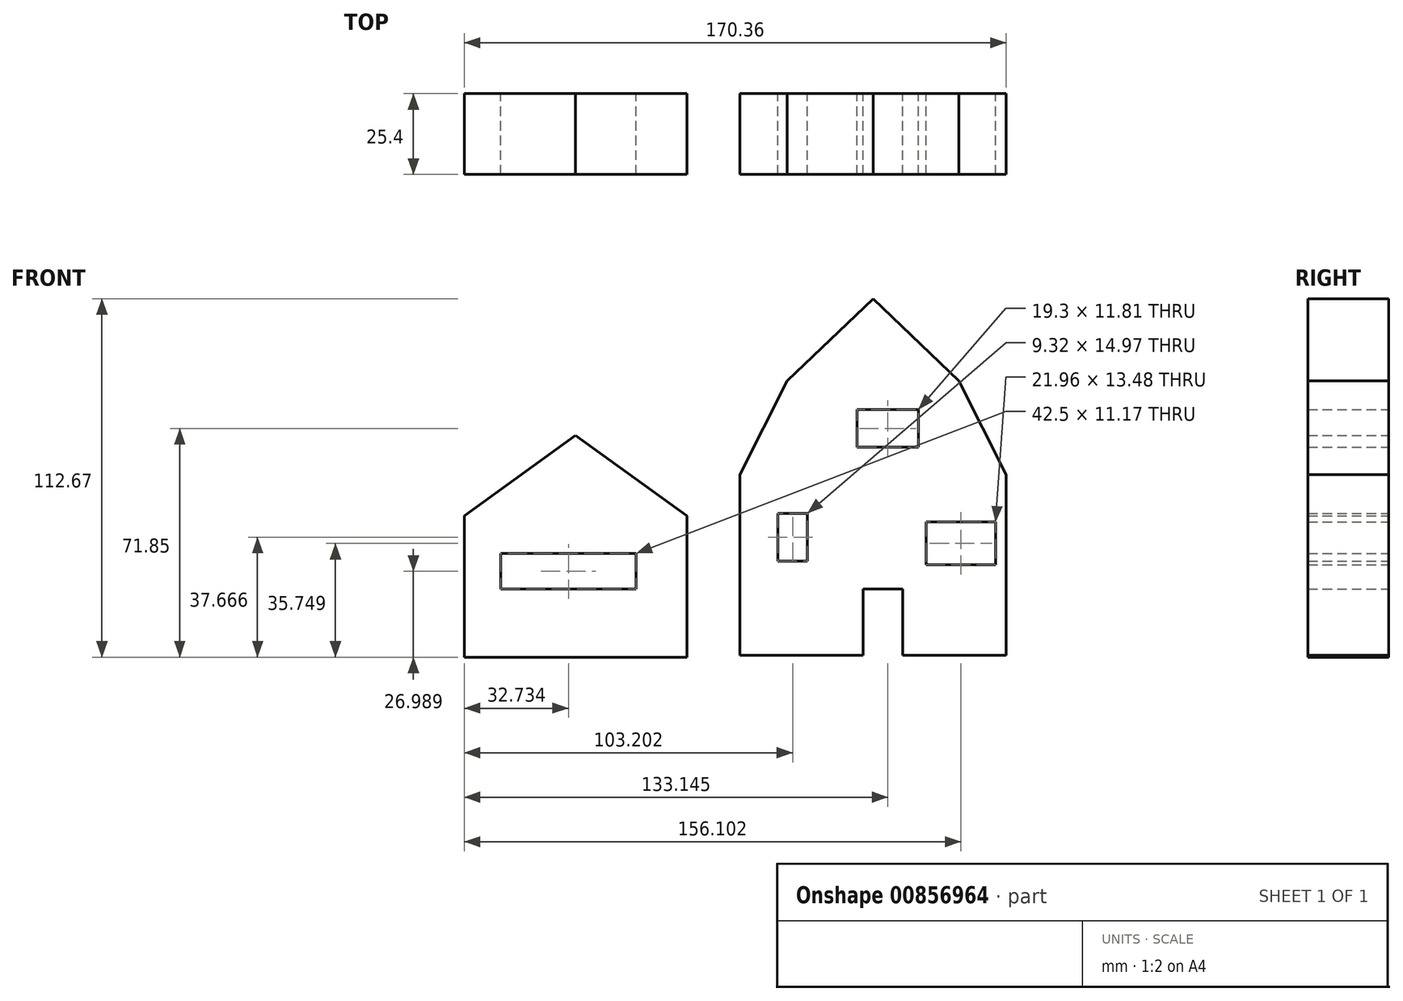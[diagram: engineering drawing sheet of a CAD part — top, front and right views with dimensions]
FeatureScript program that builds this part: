
annotation { "Feature Type Name" : "Feature", "Feature Type Description" : "" }
export const myFeature = defineFeature(function(context is Context, id is Id, definition is map)
    precondition{}
    {
        {
            var Q0;
            Q0=qCreatedBy(makeId("Front.planeOp"),FACE);
            var sketch = newSketch(context, id + "F0", { "sketchPlane" : qUnion([Q0])});
            skLineSegment(sketch, "E0.bottom", {"start": v(-4.1, 6.25) * mm, "end": v(79.64, 6.25) * mm});
            skLineSegment(sketch, "E0.top", {"start": v(-4.1, -50.52) * mm, "end": v(79.64, -50.52) * mm});
            skLineSegment(sketch, "E0.left", {"start": v(-4.1, 6.25) * mm, "end": v(-4.1, -50.52) * mm});
            skLineSegment(sketch, "E0.right", {"start": v(79.64, 6.25) * mm, "end": v(79.64, -50.52) * mm});
            skLineSegment(sketch, "E1", {"start": v(-4.1, 6.25) * mm, "end": v(10.78, 35.73) * mm});
            skLineSegment(sketch, "E2", {"start": v(10.78, 35.73) * mm, "end": v(64.75, 35.73) * mm});
            skLineSegment(sketch, "E3", {"start": v(64.75, 35.73) * mm, "end": v(79.64, 6.25) * mm});
            skLineSegment(sketch, "E4", {"start": v(10.78, 35.73) * mm, "end": v(37.76, 61.53) * mm});
            skLineSegment(sketch, "E5", {"start": v(37.76, 61.53) * mm, "end": v(64.75, 35.73) * mm});
            skLineSegment(sketch, "E6.bottom", {"start": v(-90.72, -6.78) * mm, "end": v(-20.78, -6.78) * mm});
            skLineSegment(sketch, "E6.top", {"start": v(-90.72, -51.14) * mm, "end": v(-20.78, -51.14) * mm});
            skLineSegment(sketch, "E6.left", {"start": v(-90.72, -6.78) * mm, "end": v(-90.72, -51.14) * mm});
            skLineSegment(sketch, "E6.right", {"start": v(-20.78, -6.78) * mm, "end": v(-20.78, -51.14) * mm});
            skLineSegment(sketch, "E7", {"start": v(-90.72, -6.78) * mm, "end": v(-55.75, 18.56) * mm});
            skLineSegment(sketch, "E8", {"start": v(-55.75, 18.56) * mm, "end": v(-20.78, -6.78) * mm});
            skLineSegment(sketch, "E9", {"start": v(-79.24, -51.14) * mm, "end": v(-79.24, -18.57) * mm});
            skLineSegment(sketch, "E10", {"start": v(-79.24, -18.57) * mm, "end": v(-36.74, -18.57) * mm});
            skLineSegment(sketch, "E11", {"start": v(-36.74, -18.57) * mm, "end": v(-36.74, -51.14) * mm});
            skLineSegment(sketch, "E12", {"start": v(34.67, -50.52) * mm, "end": v(34.67, -29.73) * mm});
            skLineSegment(sketch, "E13", {"start": v(34.67, -29.73) * mm, "end": v(47.08, -29.73) * mm});
            skLineSegment(sketch, "E14", {"start": v(47.08, -29.73) * mm, "end": v(47.08, -50.52) * mm});
            skLineSegment(sketch, "E15", {"start": v(-79.24, -29.74) * mm, "end": v(-36.74, -29.74) * mm});
            skLineSegment(sketch, "E16", {"start": v(-36.74, -29.74) * mm, "end": v(-45.42, -29.74) * mm});
            skLineSegment(sketch, "E17", {"start": v(-45.42, -29.74) * mm, "end": v(-45.42, -18.57) * mm});
            skLineSegment(sketch, "E18", {"start": v(-53.18, -29.74) * mm, "end": v(-53.18, -18.57) * mm});
            skLineSegment(sketch, "E19", {"start": v(-61.55, -29.74) * mm, "end": v(-61.55, -18.57) * mm});
            skLineSegment(sketch, "E20", {"start": v(-70.24, -29.74) * mm, "end": v(-70.24, -18.57) * mm});
            skLineSegment(sketch, "E21.bottom", {"start": v(32.78, 26.61) * mm, "end": v(52.07, 26.61) * mm});
            skLineSegment(sketch, "E21.top", {"start": v(32.78, 14.8) * mm, "end": v(52.07, 14.8) * mm});
            skLineSegment(sketch, "E21.left", {"start": v(32.78, 26.61) * mm, "end": v(32.78, 14.8) * mm});
            skLineSegment(sketch, "E21.right", {"start": v(52.07, 26.61) * mm, "end": v(52.07, 14.8) * mm});
            skLineSegment(sketch, "E22.bottom", {"start": v(7.82, -5.99) * mm, "end": v(17.14, -5.99) * mm});
            skLineSegment(sketch, "E22.top", {"start": v(7.82, -20.96) * mm, "end": v(17.14, -20.96) * mm});
            skLineSegment(sketch, "E22.left", {"start": v(7.82, -5.99) * mm, "end": v(7.82, -20.96) * mm});
            skLineSegment(sketch, "E22.right", {"start": v(17.14, -5.99) * mm, "end": v(17.14, -20.96) * mm});
            skPoint(sketch, "E23.oppositeSnap0", {"position": v(79.64, -22.13) * mm});
            skLineSegment(sketch, "E23.bottom", {"start": v(54.4, -8.65) * mm, "end": v(76.36, -8.65) * mm});
            skLineSegment(sketch, "E23.top", {"start": v(54.4, -22.13) * mm, "end": v(76.36, -22.13) * mm});
            skLineSegment(sketch, "E23.left", {"start": v(54.4, -8.65) * mm, "end": v(54.4, -22.13) * mm});
            skLineSegment(sketch, "E23.right", {"start": v(76.36, -8.65) * mm, "end": v(76.36, -22.13) * mm});
            skLineSegment(sketch, "E24.bottom", {"start": v(42.43, 26.61) * mm, "end": v(32.78, 26.61) * mm});
            skLineSegment(sketch, "E24.top", {"start": v(42.43, 26.61) * mm, "end": v(32.78, 26.61) * mm});
            skLineSegment(sketch, "E24.left", {"start": v(42.43, 26.61) * mm, "end": v(42.43, 26.61) * mm});
            skLineSegment(sketch, "E24.right", {"start": v(32.78, 26.61) * mm, "end": v(32.78, 26.61) * mm});
            skSolve(sketch);
        }
        {
            var Q0;
            Q0=makeQuery(id+"F0.imprint","IMPRINT",FACE,{"disambiguationData":[TD([[makeQuery(id+"F0.imprint","IMPRINT",EDGE,{"derivedFrom":sQuery(id+"F0.wireOp",EDGE,"E2")}),1.0]])]});
            var Q1;
            Q1=makeQuery(id+"F0.imprint","IMPRINT",FACE,{"disambiguationData":[TD([[makeQuery(id+"F0.imprint","IMPRINT",EDGE,{"derivedFrom":sQuery(id+"F0.wireOp",EDGE,"E6.bottom")}),1.0]])]});
            var Q2;
            Q2=makeQuery(id+"F0.imprint","IMPRINT",FACE,{"disambiguationData":[TD([[makeQuery(id+"F0.imprint","IMPRINT",EDGE,{"derivedFrom":sQuery(id+"F0.wireOp",EDGE,"E0.bottom")}),1.0]])]});
            var Q3;
            Q3=makeQuery(id+"F0.imprint","IMPRINT",FACE,{"disambiguationData":[TD([[makeQuery(id+"F0.imprint","IMPRINT",EDGE,{"derivedFrom":sQuery(id+"F0.wireOp",EDGE,"E0.bottom")}),-1.0]])]});
            var Q4;
            {var subQ1=sQuery(id+"F0.wireOp",EDGE,"E9");var subQ6=sQuery(id+"F0.wireOp",EDGE,"E6.top");var subQ8=makeQuery(id+"F0.imprint","INTERSECT",VERTEX,{"derivedFrom":[subQ6,subQ1]});Q4=makeQuery(id+"F0.imprint","IMPRINT",FACE,{"disambiguationData":[TD([[makeQuery(id+"F0.imprint","IMPRINT",EDGE,{"disambiguationData":[TD([[subQ8,-1.0]])],"derivedFrom":subQ6}),1.0]])]});}
            var Q5;
            Q5=makeQuery(id+"F0.imprint","IMPRINT",FACE,{"disambiguationData":[TD([[makeQuery(id+"F0.imprint","IMPRINT",EDGE,{"derivedFrom":sQuery(id+"F0.wireOp",EDGE,"E6.bottom")}),-1.0]])]});
            extrude(context, id + "F1", {"entities" : qUnion([Q0, Q1, Q2, Q3, Q4, Q5]), "depth" : 25.4 * mm, "offsetDistance" : 25.4 * mm});
        }
    });
